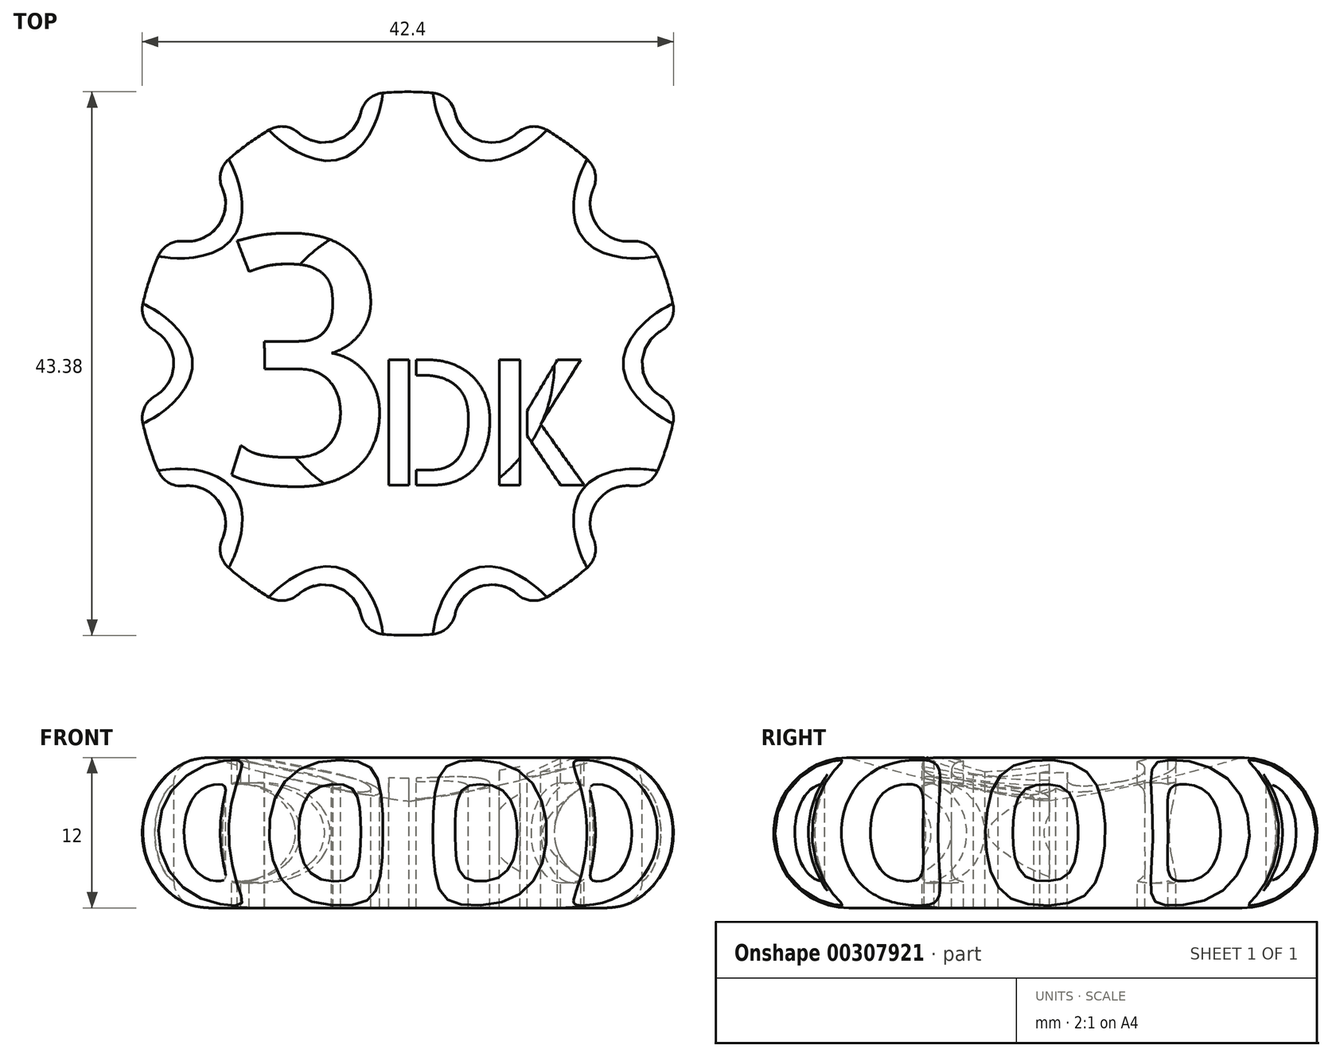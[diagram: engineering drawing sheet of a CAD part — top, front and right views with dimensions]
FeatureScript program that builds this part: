
annotation { "Feature Type Name" : "Feature", "Feature Type Description" : "" }
export const myFeature = defineFeature(function(context is Context, id is Id, definition is map)
    precondition{}
    {
        {
            var Q0;
            Q0=qCreatedBy(makeId("Front.planeOp"),FACE);
            var sketch = newSketch(context, id + "F0", { "sketchPlane" : qUnion([Q0])});
            skLineSegment(sketch, "E0", {"start": v(0, 2.5) * mm, "end": v(0, -2.5) * mm});
            skLineSegment(sketch, "E1", {"start": v(0, 0) * mm, "end": v(-15.69, 0) * mm, "construction": true});
            skArc(sketch, "E2", {"start": v(-15.69, 6) * mm, "mid": v(-21.69, 0) * mm, "end": v(-15.69, -6) * mm});
            skArc(sketch, "E3", {"start": v(-15.69, 6) * mm, "mid": v(-7.91, 3.93) * mm, "end": v(0, 2.5) * mm});
            skLineSegment(sketch, "E4", {"start": v(-15.69, -6) * mm, "end": v(0, -6) * mm});
            skLineSegment(sketch, "E5", {"start": v(0, -6) * mm, "end": v(0, -2.5) * mm});
            skSolve(sketch);
        }
        {
            var Q0;
            Q0=makeQuery(id+"F0.imprint","IMPRINT",FACE,{"disambiguationData":[TD([[makeQuery(id+"F0.imprint","IMPRINT",EDGE,{"derivedFrom":sQuery(id+"F0.wireOp",EDGE,"E0")}),-1.0]])]});
            var Q1;
            Q1=sQuery(id+"F0.wireOp",EDGE,"E0");
            revolve(context, id + "F1", {"entities" : qUnion([Q0]), "axis" : qUnion([Q1]), "revolveType" : RevolveType.FULL});
        }
        {
            var Q0;
            Q0=makeQuery(id+"F1.opRevolve","SWEPT_EDGE",EDGE,{"disambiguationData":[OSD([sQuery(id+"F0.wireOp",EDGE,"E2"),sQuery(id+"F0.wireOp",EDGE,"E3")])]});
            var Q1;
            Q1=makeQuery(id+"F1.opRevolve","SWEPT_EDGE",EDGE,{"disambiguationData":[OSD([sQuery(id+"F0.wireOp",EDGE,"E2"),sQuery(id+"F0.wireOp",EDGE,"8830ca55-4aef-4d92-925b-1c68634026530.MirrorCS")])]});
            fillet(context, id + "F2", {"entities" : qUnion([Q0, Q1]), "radius" : 1 * mm, "tangentPropagation" : true, "allowEdgeOverflow" : false});
        }
        {
            var Q0;
            Q0=qCreatedBy(makeId("Top.planeOp"),FACE);
            var sketch = newSketch(context, id + "F3", { "sketchPlane" : qUnion([Q0])});
            skText(sketch, "E6", { "text": "3", "fontName": "AllertaStencil-Regular.ttf"});
            skText(sketch, "E7", { "text": "D", "fontName": "AllertaStencil-Regular.ttf"});
            skText(sketch, "E8", { "text": "K", "fontName": "AllertaStencil-Regular.ttf"});
            const initialGuessF3  = {"E6": [-0.01607, -0.00969, 1, 0, 0.02], "E7": [-0.00283, -0.00969, 1, 0, 0.01], "E8": [0.00604, -0.00969, 1, 0, 0.01]};
            skSetInitialGuess(sketch, initialGuessF3);
            skSolve(sketch);
        }
        {
            var Q0;
            Q0 = qSketchRegion(id + "F3", true);
            var Q1;
            Q1=makeQuery(id+"F1.opRevolve","SWEPT_FACE",FACE,{"disambiguationData":[OSD([sQuery(id+"F0.wireOp",EDGE,"E3")])]});
            var Q2;
            Q2=makeQuery(id+"F1.opRevolve","SWEPT_BODY",BODY,{"disambiguationData":[OSD([sQuery(id+"F0.wireOp",EDGE,"E0"),sQuery(id+"F0.wireOp",EDGE,"E2"),sQuery(id+"F0.wireOp",EDGE,"E3"),sQuery(id+"F0.wireOp",EDGE,"8830ca55-4aef-4d92-925b-1c68634026530.MirrorCS")])]});
            var Q3;
            Q3=makeQuery(id+"F1.opRevolve","SWEPT_BODY",BODY,{"disambiguationData":[OSD([sQuery(id+"F0.wireOp",EDGE,"E0"),sQuery(id+"F0.wireOp",EDGE,"E2"),sQuery(id+"F0.wireOp",EDGE,"E3"),sQuery(id+"F0.wireOp",EDGE,"8830ca55-4aef-4d92-925b-1c68634026530.MirrorCS")])]});
            extrude(context, id + "F4", {"entities" : qUnion([Q0]), "operationType" : NewBodyOperationType.REMOVE, "endBound" : BoundingType.UP_TO_BODY, "oppositeDirection" : true, "endBoundEntityFace" : qUnion([Q1]), "endBoundEntityBody" : qUnion([Q2]), "depth" : 20 * mm, "hasSecondDirection" : true, "secondDirectionBound" : SecondDirectionBoundingType.UP_TO_BODY, "secondDirectionOppositeDirection" : false, "secondDirectionBoundEntityBody" : qUnion([Q3]), "secondDirectionDepth" : 25 * mm});
        }
        {
            var Q0;
            Q0=qCreatedBy(makeId("Front.planeOp"),FACE);
            var sketch = newSketch(context, id + "F5", { "sketchPlane" : qUnion([Q0])});
            skPoint(sketch, "E9.0", {"position": v(-15.69, 0) * mm});
            skCircle(sketch, "E10", {"center": v(-15.69, 0) * mm, "radius": 4 * mm});
            skSolve(sketch);
        }
        {
            var Q0;
            Q0 = qSketchRegion(id + "F5", true);
            var Q1;
            Q1=sQuery(id+"F0.wireOp",EDGE,"E0");
            revolve(context, id + "F6", {"operationType" : NewBodyOperationType.ADD, "entities" : qUnion([Q0]), "axis" : qUnion([Q1]), "revolveType" : RevolveType.FULL});
        }
        {
            var Q0;
            Q0=qCreatedBy(makeId("Top.planeOp"),FACE);
            var sketch = newSketch(context, id + "F7", { "sketchPlane" : qUnion([Q0])});
            skPoint(sketch, "E11.0", {"position": v(-21.69, 0) * mm});
            skCircle(sketch, "E12", {"center": v(-21.69, 0) * mm, "radius": 3 * mm});
            skCircle(sketch, "E13.1.0", {"center": v(-17.55, -12.75) * mm, "radius": 3 * mm});
            skCircle(sketch, "E13.2.0", {"center": v(-6.7, -20.63) * mm, "radius": 3 * mm});
            skCircle(sketch, "E13.3.0", {"center": v(6.7, -20.63) * mm, "radius": 3 * mm});
            skCircle(sketch, "E13.4.0", {"center": v(17.55, -12.75) * mm, "radius": 3 * mm});
            skCircle(sketch, "E13.5.0", {"center": v(21.69, 0) * mm, "radius": 3 * mm});
            skCircle(sketch, "E13.6.0", {"center": v(17.55, 12.75) * mm, "radius": 3 * mm});
            skCircle(sketch, "E13.7.0", {"center": v(6.7, 20.63) * mm, "radius": 3 * mm});
            skCircle(sketch, "E13.8.0", {"center": v(-6.7, 20.63) * mm, "radius": 3 * mm});
            skCircle(sketch, "E13.9.0", {"center": v(-17.55, 12.75) * mm, "radius": 3 * mm});
            skPoint(sketch, "E13.center", {"position": v(0, 0) * mm});
            skSolve(sketch);
        }
        {
            var Q0;
            Q0=makeQuery(id+"F7.imprint","IMPRINT",FACE,{"disambiguationData":[TD([[makeQuery(id+"F7.imprint","IMPRINT",EDGE,{"derivedFrom":sQuery(id+"F7.wireOp",EDGE,"E12")}),1.0]])]});
            var Q1;
            Q1=makeQuery(id+"F7.imprint","IMPRINT",FACE,{"disambiguationData":[TD([[makeQuery(id+"F7.imprint","IMPRINT",EDGE,{"derivedFrom":sQuery(id+"F7.wireOp",EDGE,"E13.9.0")}),1.0]])]});
            var Q2;
            Q2=makeQuery(id+"F7.imprint","IMPRINT",FACE,{"disambiguationData":[TD([[makeQuery(id+"F7.imprint","IMPRINT",EDGE,{"derivedFrom":sQuery(id+"F7.wireOp",EDGE,"E13.8.0")}),1.0]])]});
            var Q3;
            Q3=makeQuery(id+"F7.imprint","IMPRINT",FACE,{"disambiguationData":[TD([[makeQuery(id+"F7.imprint","IMPRINT",EDGE,{"derivedFrom":sQuery(id+"F7.wireOp",EDGE,"E13.7.0")}),1.0]])]});
            var Q4;
            Q4=makeQuery(id+"F7.imprint","IMPRINT",FACE,{"disambiguationData":[TD([[makeQuery(id+"F7.imprint","IMPRINT",EDGE,{"derivedFrom":sQuery(id+"F7.wireOp",EDGE,"E13.6.0")}),1.0]])]});
            var Q5;
            Q5=makeQuery(id+"F7.imprint","IMPRINT",FACE,{"disambiguationData":[TD([[makeQuery(id+"F7.imprint","IMPRINT",EDGE,{"derivedFrom":sQuery(id+"F7.wireOp",EDGE,"E13.5.0")}),1.0]])]});
            var Q6;
            Q6=makeQuery(id+"F7.imprint","IMPRINT",FACE,{"disambiguationData":[TD([[makeQuery(id+"F7.imprint","IMPRINT",EDGE,{"derivedFrom":sQuery(id+"F7.wireOp",EDGE,"E13.4.0")}),1.0]])]});
            var Q7;
            Q7=makeQuery(id+"F7.imprint","IMPRINT",FACE,{"disambiguationData":[TD([[makeQuery(id+"F7.imprint","IMPRINT",EDGE,{"derivedFrom":sQuery(id+"F7.wireOp",EDGE,"E13.3.0")}),1.0]])]});
            var Q8;
            Q8=makeQuery(id+"F7.imprint","IMPRINT",FACE,{"disambiguationData":[TD([[makeQuery(id+"F7.imprint","IMPRINT",EDGE,{"derivedFrom":sQuery(id+"F7.wireOp",EDGE,"E13.2.0")}),1.0]])]});
            var Q9;
            Q9=makeQuery(id+"F7.imprint","IMPRINT",FACE,{"disambiguationData":[TD([[makeQuery(id+"F7.imprint","IMPRINT",EDGE,{"derivedFrom":sQuery(id+"F7.wireOp",EDGE,"E13.1.0")}),1.0]])]});
            var Q10;
            Q10=makeQuery(id+"F1.opRevolve","SWEPT_BODY",BODY,{"disambiguationData":[OSD([sQuery(id+"F0.wireOp",EDGE,"E0"),sQuery(id+"F0.wireOp",EDGE,"E2"),sQuery(id+"F0.wireOp",EDGE,"E3"),sQuery(id+"F0.wireOp",EDGE,"8830ca55-4aef-4d92-925b-1c68634026530.MirrorCS")])]});
            extrude(context, id + "F8", {"entities" : qUnion([Q0, Q1, Q2, Q3, Q4, Q5, Q6, Q7, Q8, Q9]), "operationType" : NewBodyOperationType.REMOVE, "endBound" : BoundingType.THROUGH_ALL, "oppositeDirection" : true, "endBoundEntityBody" : qUnion([Q10]), "depth" : 25 * mm, "hasSecondDirection" : true, "secondDirectionBound" : SecondDirectionBoundingType.THROUGH_ALL, "secondDirectionOppositeDirection" : false, "secondDirectionDepth" : 25 * mm});
        }
        {
            var Q0;
            Q0=makeQuery(id+"F8.boolean.opBoolean","INTERSECT",EDGE,{"derivedFrom":[makeQuery(id+"F1.opRevolve","SWEPT_FACE",FACE,{"disambiguationData":[OSD([sQuery(id+"F0.wireOp",EDGE,"E2")])]}),makeQuery(id+"F8.opExtrude","SWEPT_FACE",FACE,{"disambiguationData":[OSD([sQuery(id+"F7.wireOp",EDGE,"E13.9.0")])]})]});
            var Q1;
            Q1=makeQuery(id+"F8.boolean.opBoolean","INTERSECT",EDGE,{"derivedFrom":[makeQuery(id+"F1.opRevolve","SWEPT_FACE",FACE,{"disambiguationData":[OSD([sQuery(id+"F0.wireOp",EDGE,"E2")])]}),makeQuery(id+"F8.opExtrude","SWEPT_FACE",FACE,{"disambiguationData":[OSD([sQuery(id+"F7.wireOp",EDGE,"E13.8.0")])]})]});
            var Q2;
            Q2=makeQuery(id+"F8.boolean.opBoolean","INTERSECT",EDGE,{"derivedFrom":[makeQuery(id+"F1.opRevolve","SWEPT_FACE",FACE,{"disambiguationData":[OSD([sQuery(id+"F0.wireOp",EDGE,"E2")])]}),makeQuery(id+"F8.opExtrude","SWEPT_FACE",FACE,{"disambiguationData":[OSD([sQuery(id+"F7.wireOp",EDGE,"E13.7.0")])]})]});
            var Q3;
            Q3=makeQuery(id+"F8.boolean.opBoolean","INTERSECT",EDGE,{"derivedFrom":[makeQuery(id+"F1.opRevolve","SWEPT_FACE",FACE,{"disambiguationData":[OSD([sQuery(id+"F0.wireOp",EDGE,"E2")])]}),makeQuery(id+"F8.opExtrude","SWEPT_FACE",FACE,{"disambiguationData":[OSD([sQuery(id+"F7.wireOp",EDGE,"E13.6.0")])]})]});
            var Q4;
            Q4=makeQuery(id+"F8.boolean.opBoolean","INTERSECT",EDGE,{"derivedFrom":[makeQuery(id+"F1.opRevolve","SWEPT_FACE",FACE,{"disambiguationData":[OSD([sQuery(id+"F0.wireOp",EDGE,"E2")])]}),makeQuery(id+"F8.opExtrude","SWEPT_FACE",FACE,{"disambiguationData":[OSD([sQuery(id+"F7.wireOp",EDGE,"E13.5.0")])]})]});
            var Q5;
            Q5=makeQuery(id+"F8.boolean.opBoolean","INTERSECT",EDGE,{"derivedFrom":[makeQuery(id+"F1.opRevolve","SWEPT_FACE",FACE,{"disambiguationData":[OSD([sQuery(id+"F0.wireOp",EDGE,"E2")])]}),makeQuery(id+"F8.opExtrude","SWEPT_FACE",FACE,{"disambiguationData":[OSD([sQuery(id+"F7.wireOp",EDGE,"E13.4.0")])]})]});
            var Q6;
            Q6=makeQuery(id+"F8.boolean.opBoolean","INTERSECT",EDGE,{"derivedFrom":[makeQuery(id+"F1.opRevolve","SWEPT_FACE",FACE,{"disambiguationData":[OSD([sQuery(id+"F0.wireOp",EDGE,"E2")])]}),makeQuery(id+"F8.opExtrude","SWEPT_FACE",FACE,{"disambiguationData":[OSD([sQuery(id+"F7.wireOp",EDGE,"E13.3.0")])]})]});
            var Q7;
            Q7=makeQuery(id+"F8.boolean.opBoolean","INTERSECT",EDGE,{"derivedFrom":[makeQuery(id+"F1.opRevolve","SWEPT_FACE",FACE,{"disambiguationData":[OSD([sQuery(id+"F0.wireOp",EDGE,"E2")])]}),makeQuery(id+"F8.opExtrude","SWEPT_FACE",FACE,{"disambiguationData":[OSD([sQuery(id+"F7.wireOp",EDGE,"E13.2.0")])]})]});
            var Q8;
            Q8=makeQuery(id+"F8.boolean.opBoolean","INTERSECT",EDGE,{"derivedFrom":[makeQuery(id+"F1.opRevolve","SWEPT_FACE",FACE,{"disambiguationData":[OSD([sQuery(id+"F0.wireOp",EDGE,"E2")])]}),makeQuery(id+"F8.opExtrude","SWEPT_FACE",FACE,{"disambiguationData":[OSD([sQuery(id+"F7.wireOp",EDGE,"E13.1.0")])]})]});
            var Q9;
            Q9=makeQuery(id+"F8.boolean.opBoolean","INTERSECT",EDGE,{"derivedFrom":[makeQuery(id+"F1.opRevolve","SWEPT_FACE",FACE,{"disambiguationData":[OSD([sQuery(id+"F0.wireOp",EDGE,"E2")])]}),makeQuery(id+"F8.opExtrude","SWEPT_FACE",FACE,{"disambiguationData":[OSD([sQuery(id+"F7.wireOp",EDGE,"E12")])]})]});
            fillet(context, id + "F9", {"entities" : qUnion([Q0, Q1, Q2, Q3, Q4, Q5, Q6, Q7, Q8, Q9]), "radius" : 2 * mm, "tangentPropagation" : true, "allowEdgeOverflow" : false});
        }
    });
